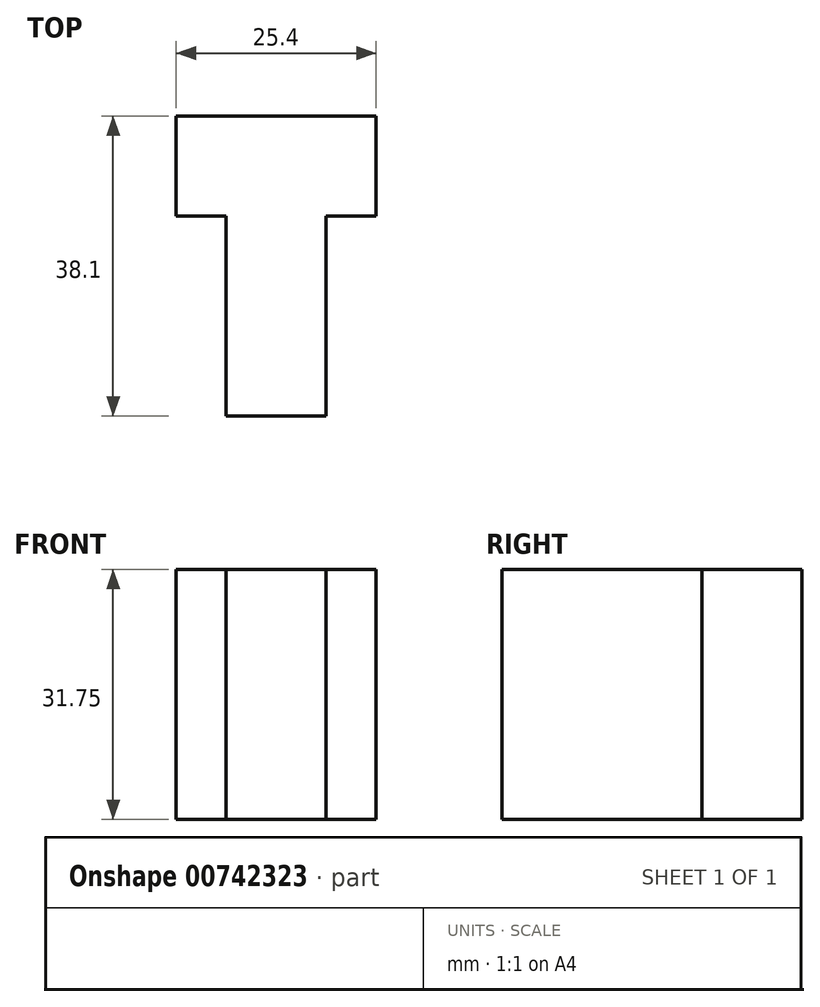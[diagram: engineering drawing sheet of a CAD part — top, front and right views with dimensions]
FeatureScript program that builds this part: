
annotation { "Feature Type Name" : "Feature", "Feature Type Description" : "" }
export const myFeature = defineFeature(function(context is Context, id is Id, definition is map)
    precondition{}
    {
        {
            var Q0;
            Q0=qCreatedBy(makeId("Top.planeOp"),FACE);
            var sketch = newSketch(context, id + "F0", { "sketchPlane" : qUnion([Q0])});
            skLineSegment(sketch, "E0", {"start": v(0, 0) * mm, "end": v(0, 25.4) * mm});
            skLineSegment(sketch, "E1", {"start": v(0, 0) * mm, "end": v(12.7, 0) * mm});
            skLineSegment(sketch, "E2", {"start": v(12.7, 0) * mm, "end": v(12.7, 25.4) * mm});
            skLineSegment(sketch, "E3", {"start": v(12.7, 25.4) * mm, "end": v(19.05, 25.4) * mm});
            skLineSegment(sketch, "E4", {"start": v(19.05, 25.4) * mm, "end": v(19.05, 38.1) * mm});
            skLineSegment(sketch, "E5", {"start": v(19.05, 38.1) * mm, "end": v(-6.35, 38.1) * mm});
            skLineSegment(sketch, "E6", {"start": v(-6.35, 38.1) * mm, "end": v(-6.35, 25.4) * mm});
            skLineSegment(sketch, "E7", {"start": v(-6.35, 25.4) * mm, "end": v(0, 25.4) * mm});
            skSolve(sketch);
        }
        {
            var Q0;
            Q0 = qSketchRegion(id + "F0", true);
            extrude(context, id + "F1", {"entities" : qUnion([Q0]), "depth" : 31.75 * mm, "offsetDistance" : 25.4 * mm});
        }
    });
